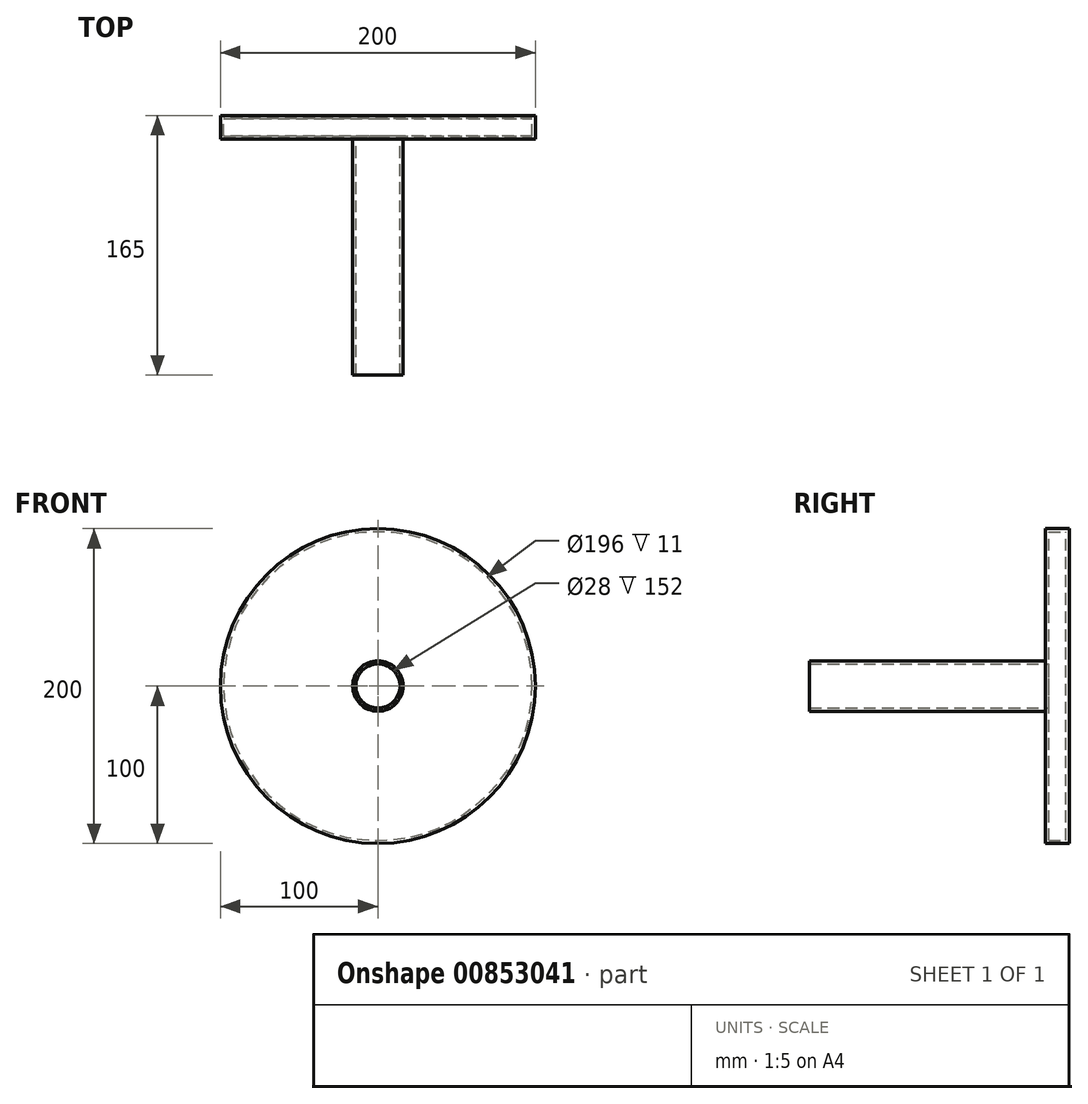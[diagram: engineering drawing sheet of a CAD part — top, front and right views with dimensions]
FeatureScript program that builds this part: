
annotation { "Feature Type Name" : "Feature", "Feature Type Description" : "" }
export const myFeature = defineFeature(function(context is Context, id is Id, definition is map)
    precondition{}
    {
        {
            var Q0;
            Q0=qCreatedBy(makeId("Front.planeOp"),FACE);
            var sketch = newSketch(context, id + "F0", { "sketchPlane" : qUnion([Q0])});
            skCircle(sketch, "E0", {"center": v(0, 0) * mm, "radius": 100 * mm});
            skSolve(sketch);
        }
        {
            var Q0;
            Q0=makeQuery(id+"F0.imprint","IMPRINT",FACE,{"disambiguationData":[TD([[makeQuery(id+"F0.imprint","IMPRINT",EDGE,{"derivedFrom":sQuery(id+"F0.wireOp",EDGE,"E0")}),1.0]])]});
            extrude(context, id + "F1", {"entities" : qUnion([Q0]), "depth" : 15 * mm, "offsetDistance" : 25 * mm});
        }
        {
            var Q0;
            Q0=makeQuery(id+"F1.opExtrude","CAP_FACE",FACE,{"disambiguationData":[OSD([sQuery(id+"F0.wireOp",EDGE,"E0")])],"isStart":false});
            var sketch = newSketch(context, id + "F2", { "sketchPlane" : qUnion([Q0])});
            skCircle(sketch, "E1", {"center": v(0, 0) * mm, "radius": 16 * mm});
            skSolve(sketch);
        }
        {
            var Q0;
            Q0=makeQuery(id+"F2.imprint","IMPRINT",FACE,{"disambiguationData":[TD([[makeQuery(id+"F2.imprint","IMPRINT",EDGE,{"derivedFrom":sQuery(id+"F2.wireOp",EDGE,"E1")}),1.0]])]});
            extrude(context, id + "F3", {"entities" : qUnion([Q0]), "operationType" : NewBodyOperationType.ADD, "depth" : 150 * mm, "offsetDistance" : 25 * mm});
        }
        {
            var Q0;
            Q0=makeQuery(id+"F3.opExtrude","CAP_FACE",FACE,{"disambiguationData":[OSD([sQuery(id+"F2.wireOp",EDGE,"E1")])],"isStart":false});
            shell(context, id + "F4", {"entities" : qUnion([Q0]), "thickness" : 2 * mm});
        }
    });
